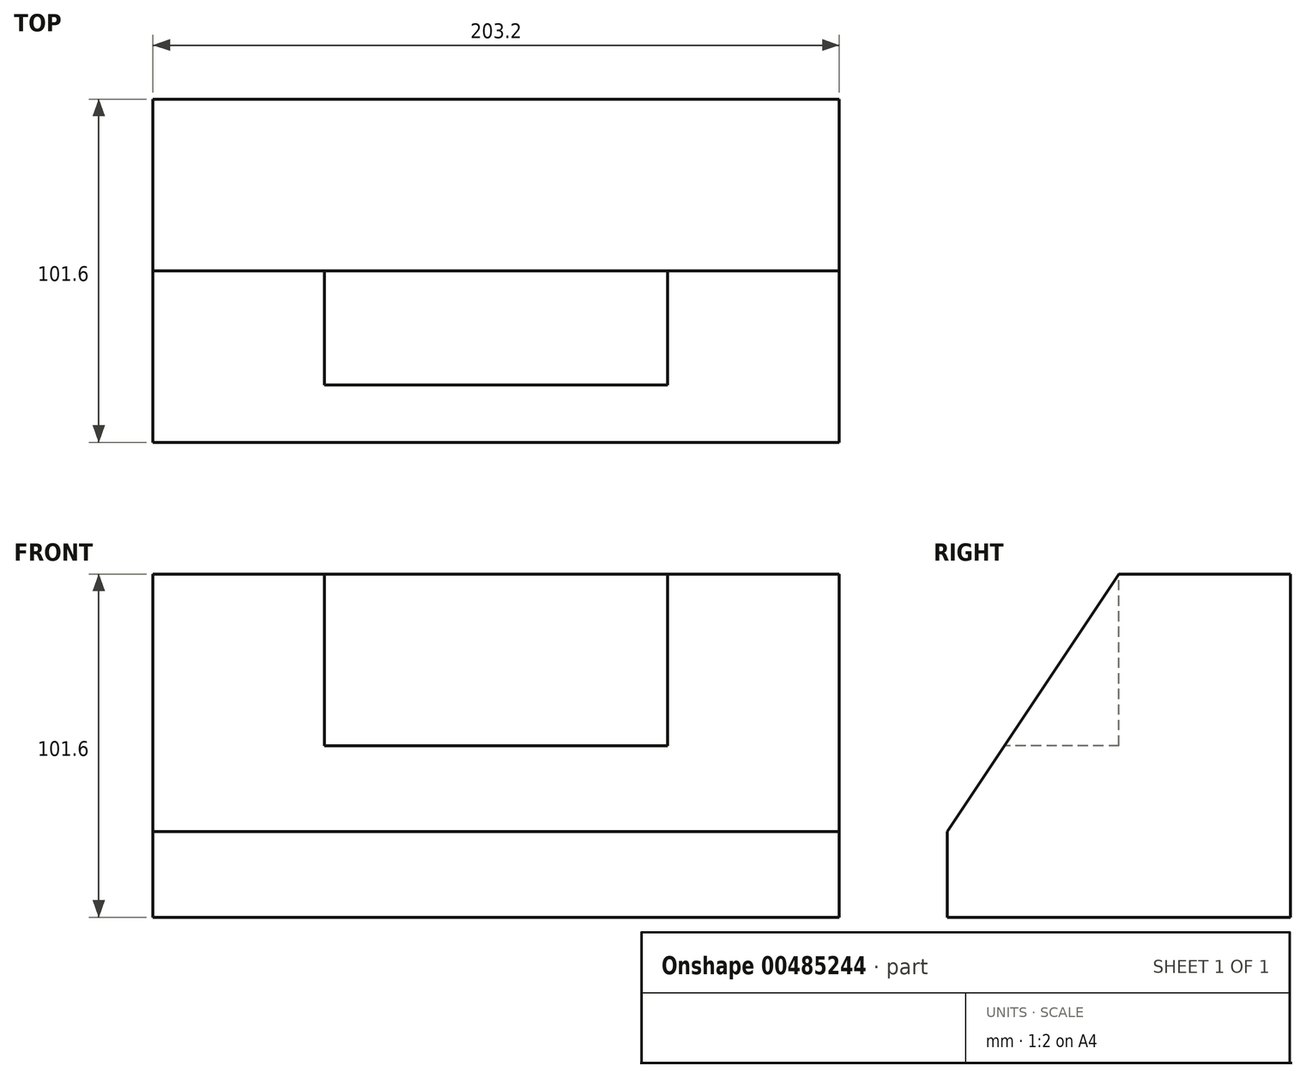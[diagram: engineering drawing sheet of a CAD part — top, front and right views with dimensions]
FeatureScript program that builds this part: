
annotation { "Feature Type Name" : "Feature", "Feature Type Description" : "" }
export const myFeature = defineFeature(function(context is Context, id is Id, definition is map)
    precondition{}
    {
        {
            var Q0;
            Q0=qCreatedBy(makeId("Front.planeOp"),FACE);
            var sketch = newSketch(context, id + "F0", { "sketchPlane" : qUnion([Q0])});
            skLineSegment(sketch, "E0.bottom", {"start": v(-106.5, 60.72) * mm, "end": v(96.7, 60.72) * mm});
            skLineSegment(sketch, "E0.top", {"start": v(-106.5, -40.88) * mm, "end": v(96.7, -40.88) * mm});
            skLineSegment(sketch, "E0.left", {"start": v(-106.5, 60.72) * mm, "end": v(-106.5, -40.88) * mm});
            skLineSegment(sketch, "E0.right", {"start": v(96.7, 60.72) * mm, "end": v(96.7, -40.88) * mm});
            skSolve(sketch);
        }
        {
            var Q0;
            Q0 = qSketchRegion(id + "F0", true);
            extrude(context, id + "F1", {"entities" : qUnion([Q0]), "depth" : 101.6 * mm});
        }
        {
            var Q0;
            Q0=makeQuery(id+"F1.opExtrude","SWEPT_FACE",FACE,{"disambiguationData":[OSD([sQuery(id+"F0.wireOp",EDGE,"E0.right")])]});
            var sketch = newSketch(context, id + "F2", { "sketchPlane" : qUnion([Q0])});
            skLineSegment(sketch, "E1", {"start": v(-101.6, -15.48) * mm, "end": v(-50.8, 60.72) * mm});
            skLineSegment(sketch, "E2", {"start": v(-50.8, 60.72) * mm, "end": v(-101.6, 60.72) * mm});
            skLineSegment(sketch, "E3", {"start": v(-101.6, 60.72) * mm, "end": v(-101.6, -15.48) * mm});
            skSolve(sketch);
        }
        {
            var Q0;
            Q0=makeQuery(id+"F2.imprint","IMPRINT",FACE,{"disambiguationData":[TD([[makeQuery(id+"F2.imprint","IMPRINT",EDGE,{"derivedFrom":sQuery(id+"F2.wireOp",EDGE,"E1")}),1.0]])]});
            extrude(context, id + "F3", {"entities" : qUnion([Q0]), "operationType" : NewBodyOperationType.REMOVE, "oppositeDirection" : true, "depth" : 203.2 * mm});
        }
        {
            var Q0;
            Q0=makeQuery(id+"F1.opExtrude","SWEPT_FACE",FACE,{"disambiguationData":[OSD([sQuery(id+"F0.wireOp",EDGE,"E0.bottom")])]});
            var sketch = newSketch(context, id + "F4", { "sketchPlane" : qUnion([Q0])});
            skLineSegment(sketch, "E4", {"start": v(-55.7, -50.8) * mm, "end": v(-55.7, -91.7) * mm});
            skLineSegment(sketch, "E5", {"start": v(-55.7, -91.7) * mm, "end": v(45.9, -91.7) * mm});
            skLineSegment(sketch, "E6", {"start": v(45.9, -91.7) * mm, "end": v(45.9, -50.8) * mm});
            skLineSegment(sketch, "E7", {"start": v(45.9, -50.8) * mm, "end": v(-55.7, -50.8) * mm});
            skSolve(sketch);
        }
        {
            var Q0;
            Q0=makeQuery(id+"F4.imprint","IMPRINT",FACE,{"disambiguationData":[TD([[makeQuery(id+"F4.imprint","IMPRINT",EDGE,{"derivedFrom":sQuery(id+"F4.wireOp",EDGE,"E4")}),1.0]])]});
            extrude(context, id + "F5", {"entities" : qUnion([Q0]), "operationType" : NewBodyOperationType.REMOVE, "oppositeDirection" : true, "depth" : 50.8 * mm});
        }
    });
